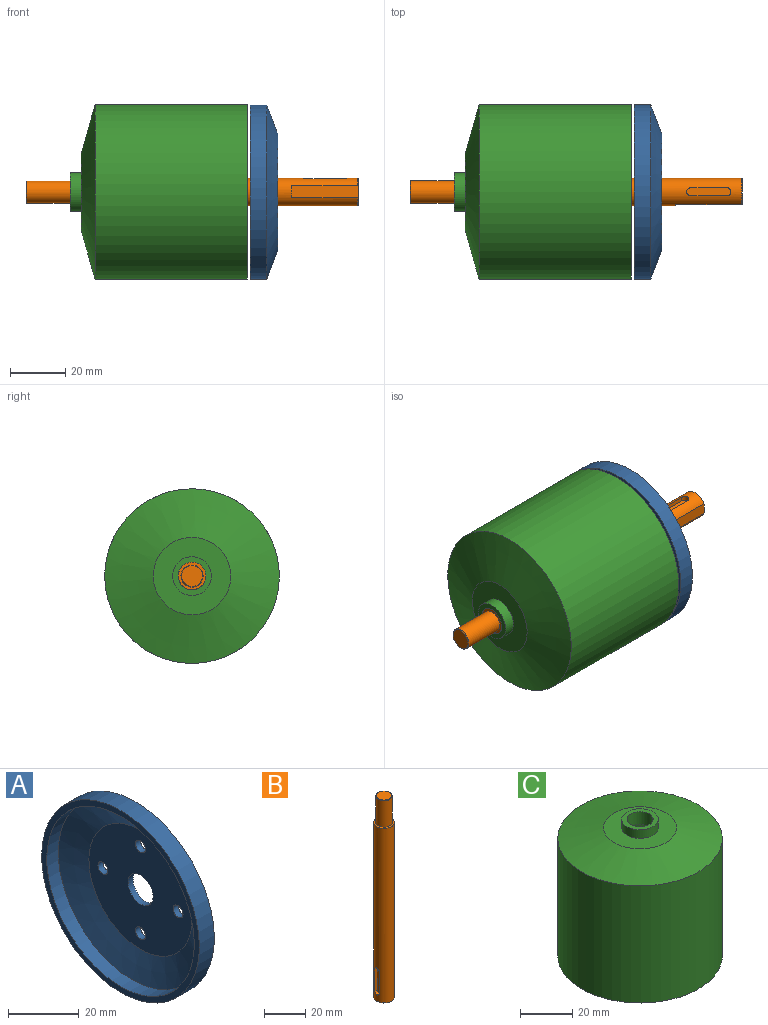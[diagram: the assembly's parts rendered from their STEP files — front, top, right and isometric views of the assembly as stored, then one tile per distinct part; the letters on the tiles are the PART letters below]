
ASSEMBLY  parts=3 mates=4
PART A: 12 faces, bbox 10x63x63 mm
  f0: cylinder r=2mm len=4mm, axis (-1,0,0), area 25.1mm2, adj f5,f11
  f1: cylinder r=2mm len=4mm, axis (-1,0,0), area 25.1mm2, adj f5,f11
  f2: cylinder r=2mm len=4mm, axis (-1,0,0), area 25.1mm2, adj f5,f11
  f3: cylinder r=2mm len=4mm, axis (-1,0,0), area 25.1mm2, adj f5,f11
  f4: cylinder r=5mm len=10mm, axis (1,0,0), area 62.8mm2, adj f5,f11
  f5: plane 41.26x41.26mm, normal (-1,0,0), area 1208.5mm2, adj f0,f1,f2,f3,f4,f6
  f6: cone r=25.07mm half-angle=69.1deg, axis (-1,0,0), area 1494.6mm2, adj f5,f7
  f7: cylinder r=29.5mm len=59mm, axis (1,0,0), area 856.6mm2, adj f6,f8
  f8: plane 63x63mm, normal (-1,0,0), area 383.3mm2, adj f7,f9
  f9: cylinder r=31.5mm len=63mm, axis (1,0,0), area 1187.5mm2, adj f8,f10
  f10: cone r=26.25mm half-angle=69.1deg, axis (-1,0,0), area 1853.2mm2, adj f9,f11
  f11: plane 42x42mm, normal (1,0,0), area 1256.6mm2, adj f0,f1,f2,f3,f4,f10
PART B: 14 faces, bbox 10x10x120 mm
  f0: plane 4.36x0.5mm, normal (0,0,-1), area 1.5mm2, adj f1,f2
  f1: plane 24.02x4.38mm, normal (0,1,0), area 104.5mm2, adj f0,f2,f12,f13
  f2: cylinder r=5mm len=103.8mm, axis (0,0,-1), area 3109.4mm2, adj f0,f1,f3,f4,f5,f6,f11,f12
  f3: cylinder r=1.5mm len=3mm, axis (1,0,0), area 7.9mm2, adj f2,f4,f5,f7
  f4: plane 13x1.57mm, normal (0,1,0), area 20.4mm2, adj f2,f3,f6,f7
  f5: plane 13x1.57mm, normal (0,-1,0), area 20.4mm2, adj f2,f3,f6,f7
  f6: cylinder r=1.5mm len=3mm, axis (1,0,0), area 7.9mm2, adj f2,f4,f5,f7
  f7: plane 16x3mm, normal (-1,0,0), area 46.1mm2, adj f3,f4,f5,f6
  f8: plane 7.6x7.6mm, normal (0,0,1), area 45.4mm2, adj f9
  f9: cone r=3.9mm half-angle=45deg, axis (0,0,-1), area 6.9mm2, adj f8,f10
  f10: cylinder r=4mm len=15.8mm, axis (0,0,-1), area 397.1mm2, adj f9,f11
  f11: plane 10x10mm, normal (0,0,1), area 28.3mm2, adj f2,f10
  f12: cone r=4.9mm half-angle=45deg, axis (0,0,1), area 7.6mm2, adj f1,f2,f13
  f13: plane 9.6x9.3mm, normal (0,0,-1), area 71.7mm2, adj f1,f12
PART C: 10 faces, bbox 63.1x63.1x64 mm
  f0: cylinder r=7mm len=14mm, axis (0,0,-1), area 175.9mm2, adj f1,f9
  f1: plane 28x28mm, normal (0,0,1), area 461.8mm2, adj f0,f2
  f2: cone r=22.78mm half-angle=74.1deg, axis (0,0,-1), area 2612.2mm2, adj f1,f3
  f3: cylinder r=31.55mm len=63.11mm, axis (0,0,-1), area 10904.5mm2, adj f2,f4
  f4: plane 63.11x63.11mm, normal (0,0,-1), area 384mm2, adj f3,f5
  f5: cylinder r=29.55mm len=59.11mm, axis (0,0,-1), area 9932.9mm2, adj f4,f6
  f6: cone r=21.64mm half-angle=74.1deg, axis (0,0,-1), area 2238.3mm2, adj f5,f7
  f7: plane 27.44x27.44mm, normal (0,0,-1), area 512.9mm2, adj f6,f8
  f8: cylinder r=5mm len=10mm, axis (0,0,-1), area 188.5mm2, adj f7,f9
  f9: plane 14x14mm, normal (0,0,1), area 75.4mm2, adj f0,f8
PLACE A rot(axis=(-1,0,0),0.6deg) t=(7.46,24.7,-21.96)mm
PLACE B rot(axis=(0.71,0,-0.71),179.6deg) t=(-73.53,24.7,-21.96)mm
PLACE C rot(axis=(0.67,-0.33,-0.67),143.4deg) t=(-57.53,24.7,-21.96)mm
MATE cylindrical A.f4 <-> B.f2  axis (-1,0,0) through (15.46,24.7,-21.96)mm
MATE planar B.f2 <-> C.f0  axis (-1,0,0) through (-57.53,24.7,-21.96)mm
MATE planar B.f2 <-> A.f1  axis (1,0,0) through (46.47,24.7,-21.96)mm
MATE cylindrical C.f0 <-> B.f2  axis (-1,0,0) through (-57.53,24.7,-21.96)mm
